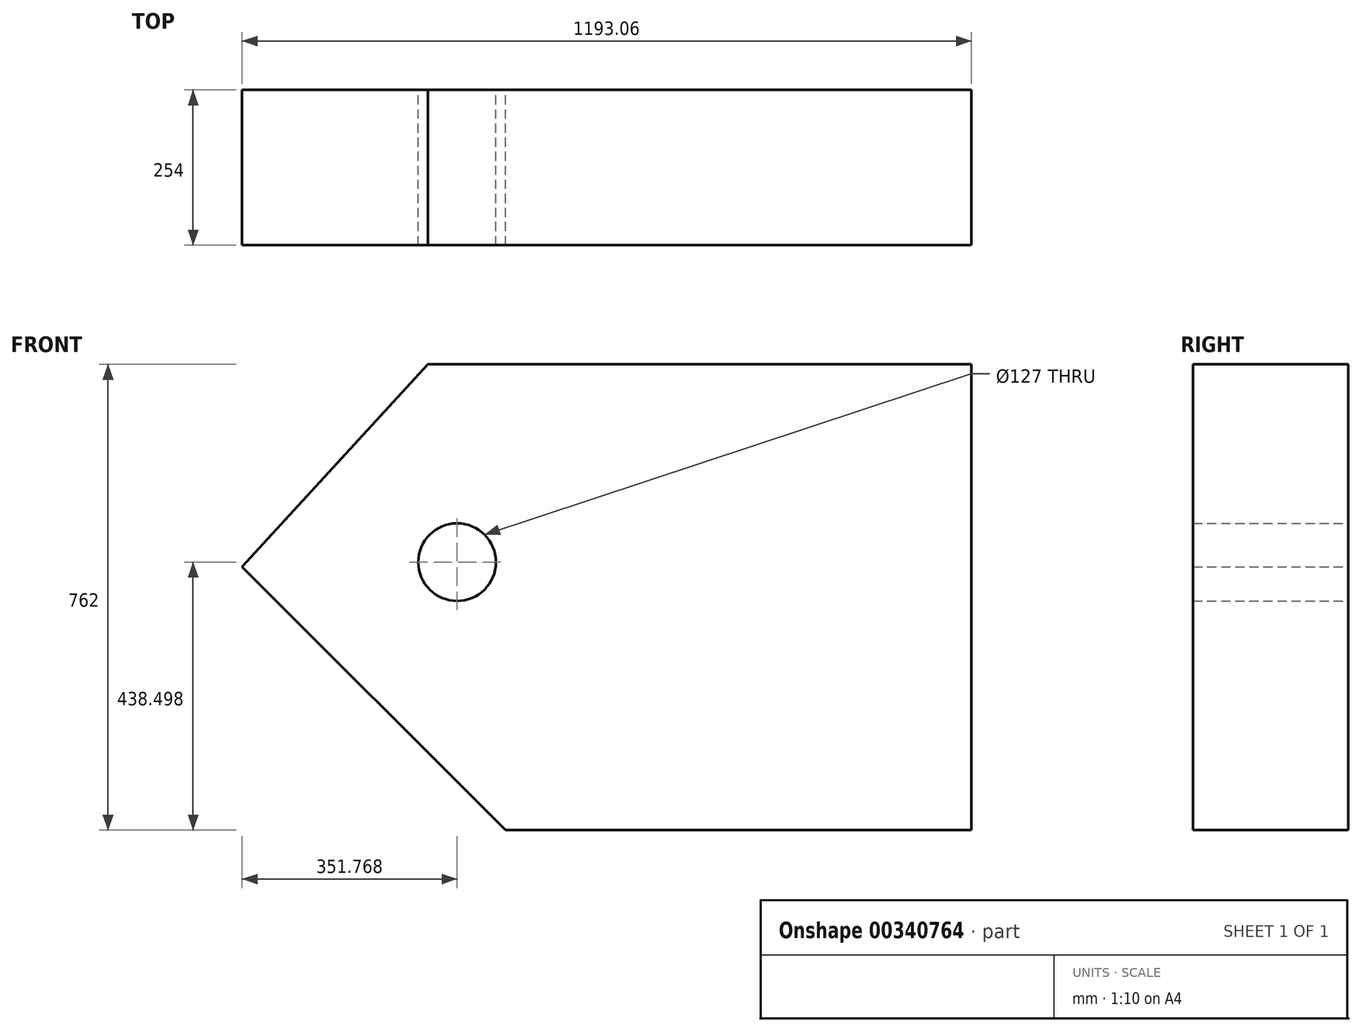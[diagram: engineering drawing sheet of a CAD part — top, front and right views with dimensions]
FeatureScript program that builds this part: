
annotation { "Feature Type Name" : "Feature", "Feature Type Description" : "" }
export const myFeature = defineFeature(function(context is Context, id is Id, definition is map)
    precondition{}
    {
        {
            var Q0;
            Q0=qCreatedBy(makeId("Front.planeOp"),FACE);
            var sketch = newSketch(context, id + "F0", { "sketchPlane" : qUnion([Q0])});
            skLineSegment(sketch, "E0", {"start": v(-207.95, 375.2) * mm, "end": v(681.05, 375.2) * mm});
            skLineSegment(sketch, "E1", {"start": v(681.05, 375.2) * mm, "end": v(681.05, -386.8) * mm});
            skLineSegment(sketch, "E2", {"start": v(681.05, -386.8) * mm, "end": v(-80.95, -386.8) * mm});
            skLineSegment(sketch, "E3", {"start": v(-80.95, -386.8) * mm, "end": v(-512, 44.25) * mm});
            skLineSegment(sketch, "E4", {"start": v(-512, 44.25) * mm, "end": v(-207.95, 375.2) * mm});
            skCircle(sketch, "E5", {"center": v(-160.24, 51.7) * mm, "radius": 63.5 * mm});
            skSolve(sketch);
        }
        {
            var Q0;
            Q0=makeQuery(id+"F0.imprint","IMPRINT",FACE,{"disambiguationData":[TD([[makeQuery(id+"F0.imprint","IMPRINT",EDGE,{"derivedFrom":sQuery(id+"F0.wireOp",EDGE,"E0")}),-1.0]])]});
            extrude(context, id + "F1", {"entities" : qUnion([Q0]), "depth" : 254 * mm});
        }
    });
